# Revit family: RPF_FSN2E_1.0_to_2.5_LOD_200
name_source: partatom
category: Equipement de génie climatique
revit_build: Autodesk Revit 2016 (Build: 20150220_1215(x64)
units: mm (PartAtom-declared; Revit-internal decimal feet)

## family parameters
Cote de connecteur circulaire = Utiliser le diamètre
Couper avec des vides une fois chargée = Non
Hôte = Face
Numéro OmniClass = 23.75.00.00
Partagée = Non
Point de calcul de pièce = Non
Titre OmniClass = Climate Control (HVAC)
Type d'élément = Normal

## types (4) — shared parameters
BC_OBJECT_ID = 6675
Color = Spring white (4.1Y8.5/0.7)
Diamètre Eau Sortie = 20 mm  [stored 0.0656168 ft]
Elévation par défaut = 1219 mm
Fabricant = HITACHI
Frequency = 50 Hz
Maximum AC Voltage = 253 V
Minimum AC Voltage = 207 V
Modèle = RPF FSN2E
Nominal Voltage = 230 V
Number of Poles = 1
Overall Depth = 220 mm
Overall Height = 630 mm  [stored 2.06693 ft]
Refrigerant = R410A (factory-charged corrosion-proof nitrogen)
Usage Current = 5 A
Void width = 157 mm  [stored 0.515092 ft]

## per-type parameters (varying)
| type | Air Flow (HiH/Hi/Me/low) m3/min | Cooling Capacity | Diamètre Eau Entrée | Diamètre Gaz Entrée | Fan motor input | Heating Capacity | Mass | Maximum Air Flow | Minimum Air Flow | Overall Width | Sound power at medium load (dB(A)) | Sound power at minimal load (dB(A)) | Sound power level (dB(A)) | Sound power max (dB(A)) |
| RPF FSN2E 1.0 | 8.5/7/6 | 3 kW | 6 mm  [stored 0.019685 ft] | 15 mm  [stored 0.0492126 ft] | 20 W | 3 kW | 25.00 kg | 8500.0 L/min | 6000.0 L/min | 1045 mm | 32 | 29 | 57 | 35 |
| RPF FSN2E 2.5 | 16/14/11 | 6 kW | 10 mm  [stored 0.0328084 ft] | 18 mm | 45 W | 6 kW | 34.00 kg | 16000.0 L/min | 11000.0 L/min | 1420 mm | 38 | 34 | 60 | 42 |
| RPF FSN2E 2.0 | 16/14/11 | 5 kW | 6 mm  [stored 0.019685 ft] | 18 mm | 45 W | 6 kW | 33.00 kg | 16000.0 L/min | 11000.0 L/min | 1420 mm | 36 | 32 | 60 | 39 |
| RPF FSN2E 1.5 | 8.5/7/6 | 4 kW | 6 mm  [stored 0.019685 ft] | 15 mm  [stored 0.0492126 ft] | 28 W | 4 kW | 28.00 kg | 8500.0 L/min | 6000.0 L/min | 1170 mm | 35 | 31 | 60 | 38 |

note: [stored X ft] marks values corroborated as IEEE doubles in the binary element streams (Revit-internal decimal feet)

## geometry (parser evidence)
native form markers: Blend x2
no freeform markers — native parametric forms only
